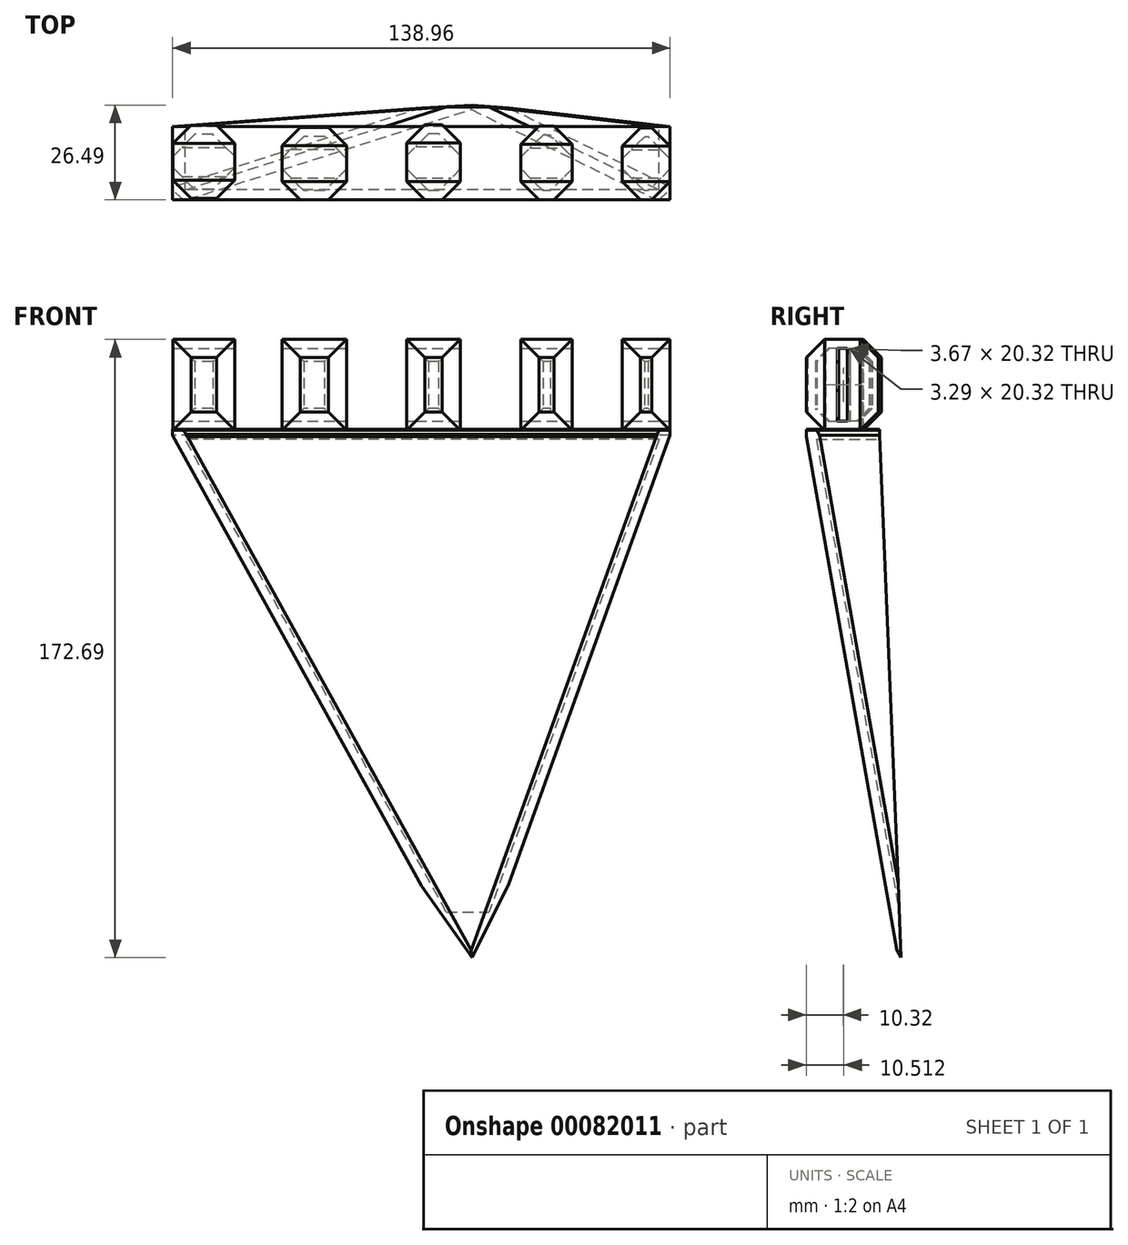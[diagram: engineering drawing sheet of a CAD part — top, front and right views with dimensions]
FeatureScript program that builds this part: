
annotation { "Feature Type Name" : "Feature", "Feature Type Description" : "" }
export const myFeature = defineFeature(function(context is Context, id is Id, definition is map)
    precondition{}
    {
        {
            var Q0;
            Q0=qCreatedBy(makeId("Top.planeOp"),FACE);
            var sketch = newSketch(context, id + "F0", { "sketchPlane" : qUnion([Q0])});
            skLineSegment(sketch, "E0.bottom", {"start": v(-73.3, 52.6) * mm, "end": v(-56.02, 52.6) * mm});
            skLineSegment(sketch, "E0.top", {"start": v(-73.3, 73.05) * mm, "end": v(-56.02, 73.05) * mm});
            skLineSegment(sketch, "E0.left", {"start": v(-73.3, 52.6) * mm, "end": v(-73.3, 73.05) * mm});
            skLineSegment(sketch, "E0.right", {"start": v(-56.02, 52.6) * mm, "end": v(-56.02, 73.05) * mm});
            skSolve(sketch);
        }
        {
            var Q0;
            Q0=qCreatedBy(makeId("Top.planeOp"),FACE);
            var sketch = newSketch(context, id + "F1", { "sketchPlane" : qUnion([Q0])});
            skLineSegment(sketch, "E1.bottom", {"start": v(-42.85, 52.23) * mm, "end": v(-24.82, 52.23) * mm});
            skLineSegment(sketch, "E1.top", {"start": v(-42.85, 72.51) * mm, "end": v(-24.82, 72.51) * mm});
            skLineSegment(sketch, "E1.left", {"start": v(-42.85, 52.23) * mm, "end": v(-42.85, 72.51) * mm});
            skLineSegment(sketch, "E1.right", {"start": v(-24.82, 52.23) * mm, "end": v(-24.82, 72.51) * mm});
            skLineSegment(sketch, "E2.bottom", {"start": v(-8.02, 52.23) * mm, "end": v(7.01, 52.23) * mm});
            skLineSegment(sketch, "E2.top", {"start": v(-8.02, 73.25) * mm, "end": v(7.01, 73.25) * mm});
            skLineSegment(sketch, "E2.left", {"start": v(-8.02, 52.23) * mm, "end": v(-8.02, 73.25) * mm});
            skLineSegment(sketch, "E2.right", {"start": v(7.01, 52.23) * mm, "end": v(7.01, 73.25) * mm});
            skLineSegment(sketch, "E3.bottom", {"start": v(23.92, 52.23) * mm, "end": v(38.22, 52.23) * mm});
            skLineSegment(sketch, "E3.top", {"start": v(23.92, 72.87) * mm, "end": v(38.22, 72.87) * mm});
            skLineSegment(sketch, "E3.left", {"start": v(23.92, 52.23) * mm, "end": v(23.92, 72.87) * mm});
            skLineSegment(sketch, "E3.right", {"start": v(38.22, 52.23) * mm, "end": v(38.22, 72.87) * mm});
            skLineSegment(sketch, "E4.bottom", {"start": v(52.23, 52.23) * mm, "end": v(65.57, 52.23) * mm});
            skLineSegment(sketch, "E4.top", {"start": v(52.23, 72.37) * mm, "end": v(65.57, 72.37) * mm});
            skLineSegment(sketch, "E4.left", {"start": v(52.23, 52.23) * mm, "end": v(52.23, 72.37) * mm});
            skLineSegment(sketch, "E4.right", {"start": v(65.57, 52.23) * mm, "end": v(65.57, 72.37) * mm});
            skSolve(sketch);
        }
        {
            var Q0;
            Q0=makeQuery(id+"F1.imprint","IMPRINT",FACE,{"disambiguationData":[TD([[makeQuery(id+"F1.imprint","IMPRINT",EDGE,{"derivedFrom":sQuery(id+"F1.wireOp",EDGE,"E4.bottom")}),1.0]])]});
            extrude(context, id + "F2", {"entities" : qUnion([Q0]), "depth" : 25.4 * mm});
        }
        {
            var Q0;
            Q0=makeQuery(id+"F0.imprint","IMPRINT",FACE,{"disambiguationData":[TD([[makeQuery(id+"F0.imprint","IMPRINT",EDGE,{"derivedFrom":sQuery(id+"F0.wireOp",EDGE,"E0.bottom")}),1.0]])]});
            extrude(context, id + "F3", {"entities" : qUnion([Q0]), "depth" : 25.4 * mm});
        }
        {
            var Q0;
            Q0=makeQuery(id+"F1.imprint","IMPRINT",FACE,{"disambiguationData":[TD([[makeQuery(id+"F1.imprint","IMPRINT",EDGE,{"derivedFrom":sQuery(id+"F1.wireOp",EDGE,"E3.bottom")}),1.0]])]});
            var Q1;
            Q1=makeQuery(id+"F1.imprint","IMPRINT",FACE,{"disambiguationData":[TD([[makeQuery(id+"F1.imprint","IMPRINT",EDGE,{"derivedFrom":sQuery(id+"F1.wireOp",EDGE,"E1.bottom")}),1.0]])]});
            var Q2;
            Q2=makeQuery(id+"F1.imprint","IMPRINT",FACE,{"disambiguationData":[TD([[makeQuery(id+"F1.imprint","IMPRINT",EDGE,{"derivedFrom":sQuery(id+"F1.wireOp",EDGE,"E2.bottom")}),1.0]])]});
            extrude(context, id + "F4", {"entities" : qUnion([Q0, Q1, Q2]), "depth" : 25.4 * mm});
        }
        {
            var Q0;
            Q0=qCreatedBy(makeId("Top.planeOp"),FACE);
            var sketch = newSketch(context, id + "F5", { "sketchPlane" : qUnion([Q0])});
            skLineSegment(sketch, "E5.bottom", {"start": v(65.58, 52.27) * mm, "end": v(-73.38, 52.27) * mm});
            skLineSegment(sketch, "E5.top", {"start": v(65.58, 72.68) * mm, "end": v(-73.38, 72.68) * mm});
            skLineSegment(sketch, "E5.left", {"start": v(65.58, 52.27) * mm, "end": v(65.58, 72.68) * mm});
            skLineSegment(sketch, "E5.right", {"start": v(-73.38, 52.27) * mm, "end": v(-73.38, 72.68) * mm});
            skSolve(sketch);
        }
        {
            var Q0;
            Q0=makeQuery(id+"F5.imprint","IMPRINT",FACE,{"disambiguationData":[TD([[makeQuery(id+"F5.imprint","IMPRINT",EDGE,{"derivedFrom":sQuery(id+"F5.wireOp",EDGE,"E5.bottom")}),-1.0]])]});
            extrude(context, id + "F6", {"entities" : qUnion([Q0]), "depth" : 0.25 * mm});
        }
        {
            var Q0;
            Q0=makeQuery(id+"F6.opExtrude","CAP_FACE",FACE,{"disambiguationData":[OSD([sQuery(id+"F5.wireOp",EDGE,"E5.bottom"),sQuery(id+"F5.wireOp",EDGE,"E5.top"),sQuery(id+"F5.wireOp",EDGE,"E5.left"),sQuery(id+"F5.wireOp",EDGE,"E5.right")])],"isStart":true});
            extrude(context, id + "F7", {"entities" : qUnion([Q0]), "depth" : 1.38 * mm});
        }
        {
            var Q0;
            Q0=makeQuery(id+"F4.opExtrude","SWEPT_FACE",FACE,{"disambiguationData":[OSD([sQuery(id+"F1.wireOp",EDGE,"E2.bottom")])]});
            var Q1;
            Q1=makeQuery(id+"F2.opExtrude","SWEPT_FACE",FACE,{"disambiguationData":[OSD([sQuery(id+"F1.wireOp",EDGE,"E4.top")])]});
            var Q2;
            Q2=makeQuery(id+"F4.opExtrude","SWEPT_FACE",FACE,{"disambiguationData":[OSD([sQuery(id+"F1.wireOp",EDGE,"E3.bottom")])]});
            var Q3;
            Q3=makeQuery(id+"F3.opExtrude","SWEPT_FACE",FACE,{"disambiguationData":[OSD([sQuery(id+"F0.wireOp",EDGE,"E0.bottom")])]});
            var Q4;
            Q4=makeQuery(id+"F4.opExtrude","SWEPT_FACE",FACE,{"disambiguationData":[OSD([sQuery(id+"F1.wireOp",EDGE,"E1.top")])]});
            var Q5;
            Q5=makeQuery(id+"F4.opExtrude","SWEPT_FACE",FACE,{"disambiguationData":[OSD([sQuery(id+"F1.wireOp",EDGE,"E3.top")])]});
            var Q6;
            Q6=makeQuery(id+"F4.opExtrude","SWEPT_FACE",FACE,{"disambiguationData":[OSD([sQuery(id+"F1.wireOp",EDGE,"E2.top")])]});
            var Q7;
            Q7=makeQuery(id+"F4.opExtrude","SWEPT_FACE",FACE,{"disambiguationData":[OSD([sQuery(id+"F1.wireOp",EDGE,"E1.bottom")])]});
            var Q8;
            Q8=makeQuery(id+"F2.opExtrude","SWEPT_FACE",FACE,{"disambiguationData":[OSD([sQuery(id+"F1.wireOp",EDGE,"E4.bottom")])]});
            var Q9;
            Q9=makeQuery(id+"F3.opExtrude","SWEPT_FACE",FACE,{"disambiguationData":[OSD([sQuery(id+"F0.wireOp",EDGE,"E0.top")])]});
            chamfer(context, id + "F8", {"entities" : qUnion([Q0, Q1, Q2, Q3, Q4, Q5, Q6, Q7, Q8, Q9]), "width" : 5.08 * mm, "tangentPropagation" : true});
        }
        {
            var Q0;
            Q0=makeQuery(id+"F3.opExtrude","SWEPT_FACE",FACE,{"disambiguationData":[OSD([sQuery(id+"F0.wireOp",EDGE,"E0.left")])]});
            var Q1;
            Q1=makeQuery(id+"F2.opExtrude","SWEPT_FACE",FACE,{"disambiguationData":[OSD([sQuery(id+"F1.wireOp",EDGE,"E4.right")])]});
            var Q2;
            Q2=makeQuery(id+"F4.opExtrude","SWEPT_FACE",FACE,{"disambiguationData":[OSD([sQuery(id+"F1.wireOp",EDGE,"E2.left")])]});
            var Q3;
            Q3=makeQuery(id+"F4.opExtrude","SWEPT_FACE",FACE,{"disambiguationData":[OSD([sQuery(id+"F1.wireOp",EDGE,"E2.right")])]});
            var Q4;
            Q4=makeQuery(id+"F4.opExtrude","SWEPT_FACE",FACE,{"disambiguationData":[OSD([sQuery(id+"F1.wireOp",EDGE,"E1.left")])]});
            var Q5;
            Q5=makeQuery(id+"F3.opExtrude","SWEPT_FACE",FACE,{"disambiguationData":[OSD([sQuery(id+"F0.wireOp",EDGE,"E0.right")])]});
            var Q6;
            Q6=makeQuery(id+"F4.opExtrude","SWEPT_FACE",FACE,{"disambiguationData":[OSD([sQuery(id+"F1.wireOp",EDGE,"E1.right")])]});
            var Q7;
            Q7=makeQuery(id+"F4.opExtrude","SWEPT_FACE",FACE,{"disambiguationData":[OSD([sQuery(id+"F1.wireOp",EDGE,"E3.right")])]});
            var Q8;
            Q8=makeQuery(id+"F4.opExtrude","SWEPT_FACE",FACE,{"disambiguationData":[OSD([sQuery(id+"F1.wireOp",EDGE,"E3.left")])]});
            var Q9;
            Q9=makeQuery(id+"F2.opExtrude","SWEPT_FACE",FACE,{"disambiguationData":[OSD([sQuery(id+"F1.wireOp",EDGE,"E4.left")])]});
            shell(context, id + "F9", {"entities" : qUnion([Q0, Q1, Q2, Q3, Q4, Q5, Q6, Q7, Q8, Q9]), "thickness" : 2.54 * mm});
        }
        {
            var Q0;
            Q0=makeQuery(id+"F7.opExtrude","CAP_FACE",FACE,{"disambiguationData":[OSD([sQuery(id+"F5.wireOp",EDGE,"E5.bottom"),sQuery(id+"F5.wireOp",EDGE,"E5.top"),sQuery(id+"F5.wireOp",EDGE,"E5.left"),sQuery(id+"F5.wireOp",EDGE,"E5.right")])],"isStart":false});
            cPlane(context, id + "F10", {"entities" : qUnion([Q0]), "cplaneType" : CPlaneType.OFFSET, "offset" : 152.4 * mm, "width" : 152.4 * mm, "height" : 152.4 * mm});
        }
        {
            var Q0;
            Q0=qCreatedBy(id+"F10.planeOp",FACE);
            var sketch = newSketch(context, id + "F11", { "sketchPlane" : qUnion([Q0])});
            skPoint(sketch, "E6", {"position": v(10.79, -79) * mm});
            skSolve(sketch);
        }
        {
            var Q1;
            Q1=makeQuery(id+"F7.opExtrude","CAP_FACE",FACE,{"disambiguationData":[OSD([sQuery(id+"F5.wireOp",EDGE,"E5.bottom"),sQuery(id+"F5.wireOp",EDGE,"E5.top"),sQuery(id+"F5.wireOp",EDGE,"E5.left"),sQuery(id+"F5.wireOp",EDGE,"E5.right")])],"isStart":false});
            var Q2;
            Q2=sQuery(id+"F11.wireOp",VERTEX,"E6");
            loft(context, id + "F12", {"operationType" : NewBodyOperationType.ADD, "sheetProfilesArray" : [{ "sheetProfileEntities" : qUnion([Q1]) }, { "sheetProfileEntities" : qUnion([Q2]) }]});
        }
        {
            var Q0;
            Q0=makeQuery(id+"F12.opLoft","SWEPT_FACE",FACE,{"disambiguationData":[OSD([sQuery(id+"F5.wireOp",EDGE,"E5.top"),sQuery(id+"F5.wireOp",EDGE,"E5.left"),sQuery(id+"F5.wireOp",EDGE,"E5.right")])]});
            shell(context, id + "F13", {"entities" : qUnion([Q0]), "thickness" : 2.54 * mm});
        }
        {
            var Q0;
            Q0=makeQuery(id+"F12.opLoft","SWEPT_FACE",FACE,{"disambiguationData":[OSD([sQuery(id+"F5.wireOp",EDGE,"E5.bottom"),sQuery(id+"F5.wireOp",EDGE,"E5.left"),sQuery(id+"F5.wireOp",EDGE,"E5.right")])]});
            chamfer(context, id + "F14", {"entities" : qUnion([Q0]), "width" : 3.8 * mm, "tangentPropagation" : true});
        }
    });
